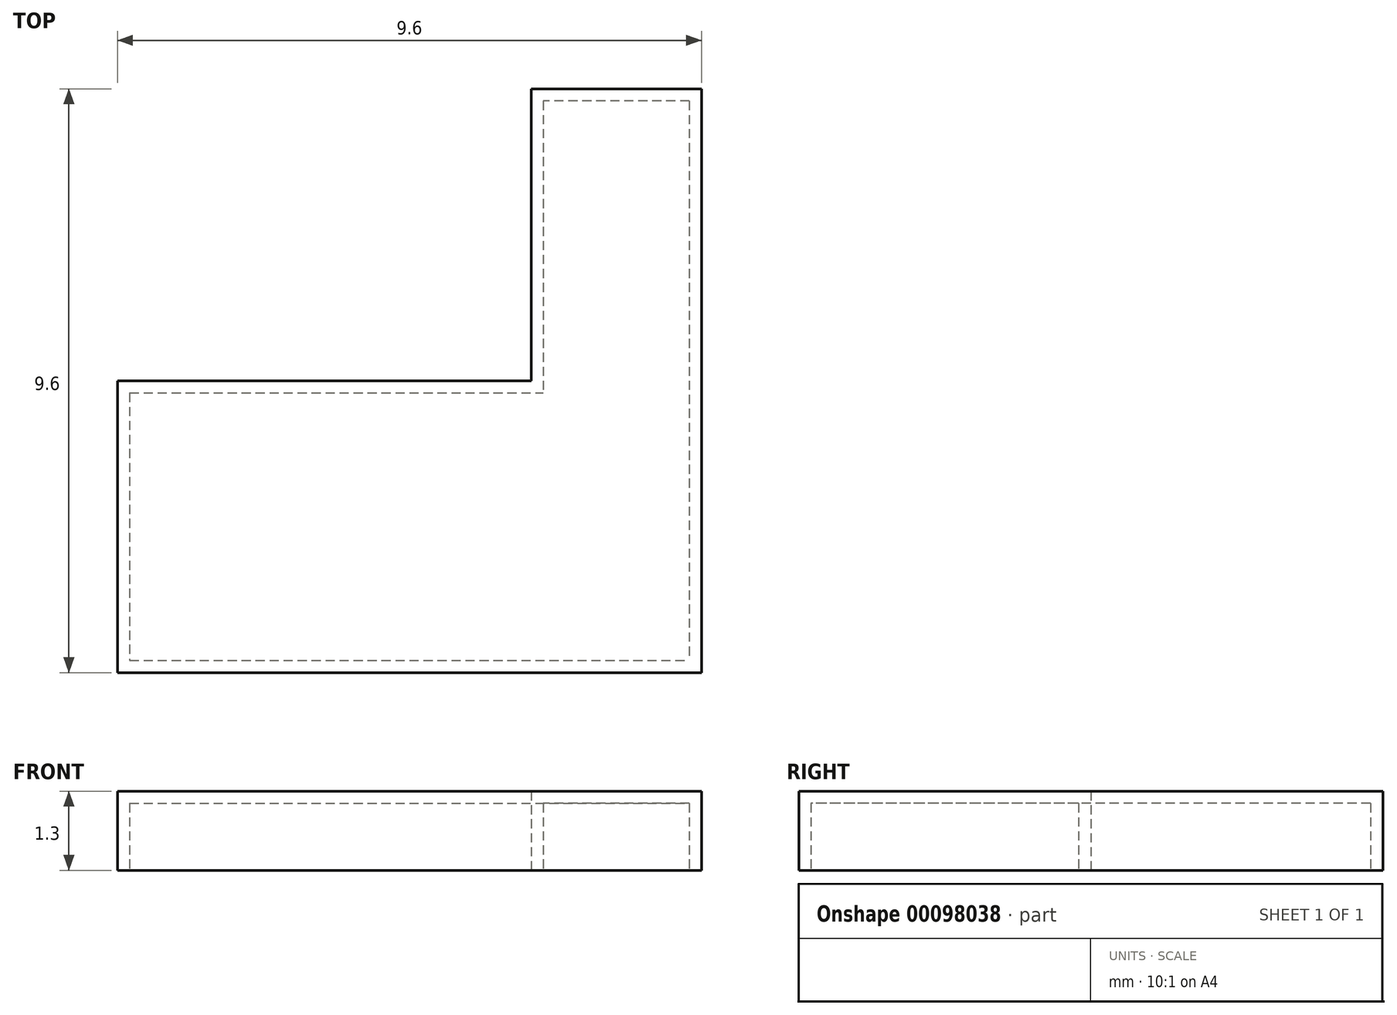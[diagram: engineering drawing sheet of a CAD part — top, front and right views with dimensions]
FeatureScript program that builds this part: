
annotation { "Feature Type Name" : "Feature", "Feature Type Description" : "" }
export const myFeature = defineFeature(function(context is Context, id is Id, definition is map)
    precondition{}
    {
        {
            var Q0;
            Q0=qCreatedBy(makeId("Top.planeOp"),FACE);
            var sketch = newSketch(context, id + "F0", { "sketchPlane" : qUnion([Q0])});
            skPoint(sketch, "E0.positionSnap0", {"position": v(0, 0) * mm});
            skLineSegment(sketch, "E1.bottom", {"start": v(-5, 5) * mm, "end": v(5, 5) * mm});
            skLineSegment(sketch, "E1.top", {"start": v(-5, -5) * mm, "end": v(5, -5) * mm});
            skLineSegment(sketch, "E1.left", {"start": v(-5, 5) * mm, "end": v(-5, -5) * mm});
            skLineSegment(sketch, "E1.right", {"start": v(5, 5) * mm, "end": v(5, -5) * mm});
            skLineSegment(sketch, "E2", {"start": v(-5, 5) * mm, "end": v(5, -5) * mm, "construction": true});
            skLineSegment(sketch, "E3", {"start": v(-5, -5) * mm, "end": v(5, 5) * mm, "construction": true});
            skLineSegment(sketch, "E4.bottom", {"start": v(-5, 5) * mm, "end": v(2, 5) * mm});
            skLineSegment(sketch, "E4.top", {"start": v(-5, 0) * mm, "end": v(2, 0) * mm});
            skLineSegment(sketch, "E4.left", {"start": v(-5, 5) * mm, "end": v(-5, 0) * mm});
            skLineSegment(sketch, "E4.right", {"start": v(2, 5) * mm, "end": v(2, 0) * mm});
            skLineSegment(sketch, "E5", {"start": v(-4.8, 0) * mm, "end": v(-4.8, -5) * mm});
            skLineSegment(sketch, "E6", {"start": v(-5, -4.8) * mm, "end": v(5, -4.8) * mm});
            skLineSegment(sketch, "E7", {"start": v(4.8, 5) * mm, "end": v(4.8, -5) * mm});
            skLineSegment(sketch, "E8", {"start": v(5, 4.8) * mm, "end": v(2, 4.8) * mm});
            skSolve(sketch);
        }
        {
            var Q0;
            {var subQ5=sQuery(id+"F0.wireOp",EDGE,"E4.top");var subQ7=sQuery(id+"F0.wireOp",EDGE,"E4.right");var subQ8=makeQuery(id+"F0.imprint","INTERSECT",VERTEX,{"derivedFrom":[subQ5,subQ7]});Q0=makeQuery(id+"F0.imprint","IMPRINT",FACE,{"disambiguationData":[TD([[makeQuery(id+"F0.imprint","IMPRINT",EDGE,{"disambiguationData":[TD([[subQ8,1.0]])],"derivedFrom":subQ5}),-1.0]])]});}
            extrude(context, id + "F1", {"entities" : qUnion([Q0]), "depth" : 1.3 * mm});
        }
        {
            var Q0;
            Q0=makeQuery(id+"F1.opExtrude","CAP_FACE",FACE,{"disambiguationData":[OSD([sQuery(id+"F0.wireOp",EDGE,"E4.top"),sQuery(id+"F0.wireOp",EDGE,"E4.right"),sQuery(id+"F0.wireOp",EDGE,"E5"),sQuery(id+"F0.wireOp",EDGE,"E6"),sQuery(id+"F0.wireOp",EDGE,"E7"),sQuery(id+"F0.wireOp",EDGE,"E8")])],"isStart":true});
            shell(context, id + "F2", {"entities" : qUnion([Q0]), "thickness" : 0.2 * mm});
        }
    });
